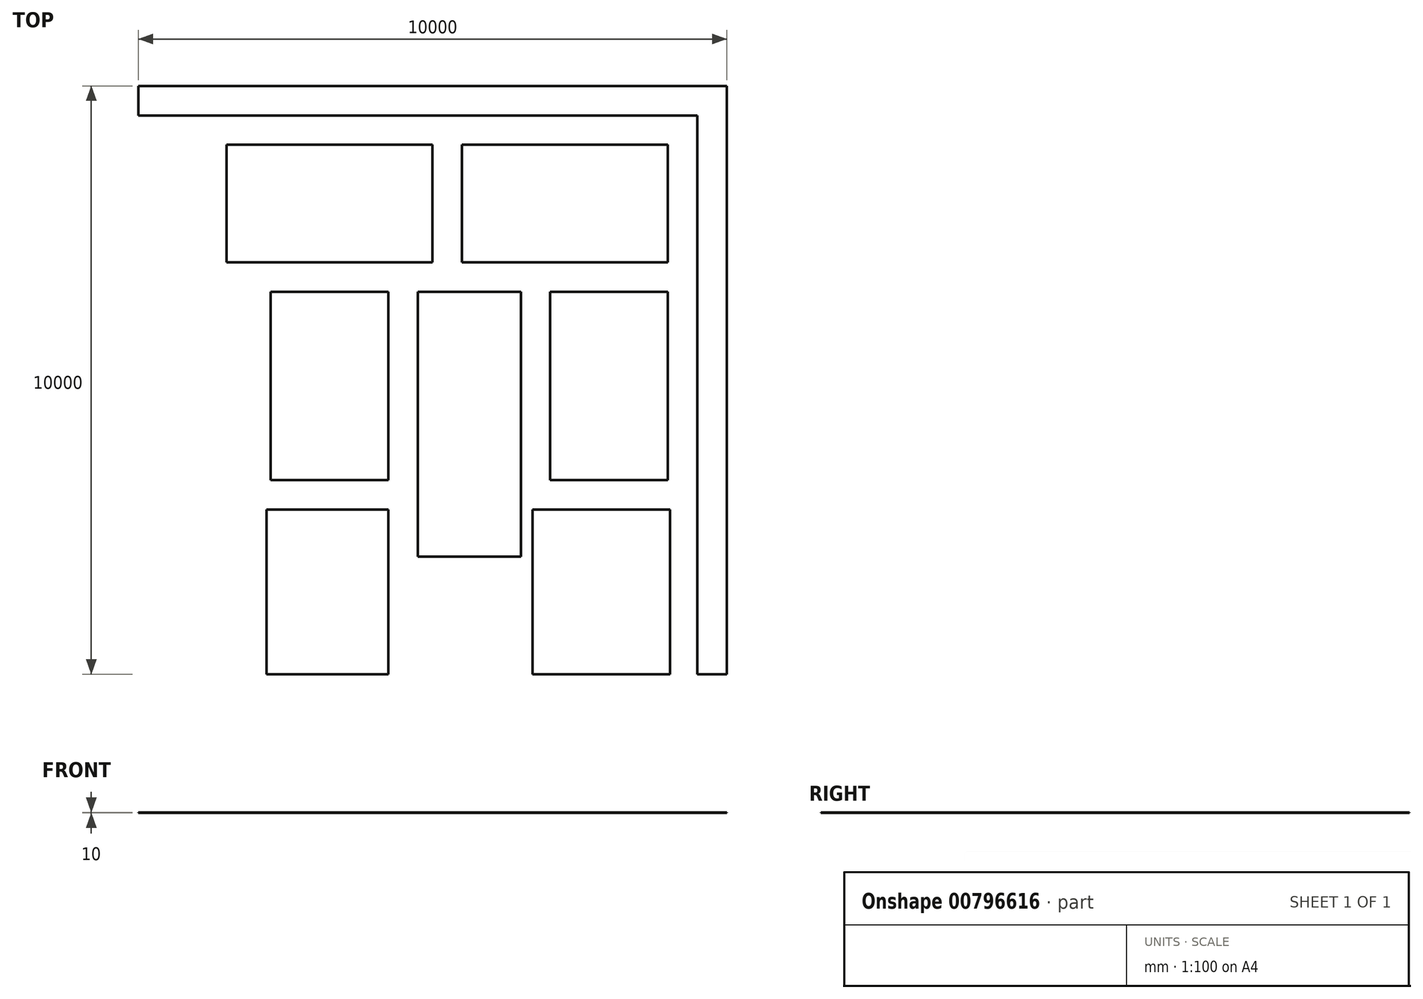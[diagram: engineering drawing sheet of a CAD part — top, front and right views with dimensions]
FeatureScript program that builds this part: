
annotation { "Feature Type Name" : "Feature", "Feature Type Description" : "" }
export const myFeature = defineFeature(function(context is Context, id is Id, definition is map)
    precondition{}
    {
        {
            var Q0;
            Q0=qCreatedBy(makeId("Top.planeOp"),FACE);
            var sketch = newSketch(context, id + "F0", { "sketchPlane" : qUnion([Q0])});
            skLineSegment(sketch, "E0.bottom", {"start": v(5000, -5000) * mm, "end": v(-5000, -5000) * mm});
            skLineSegment(sketch, "E0.top", {"start": v(5000, 5000) * mm, "end": v(-5000, 5000) * mm});
            skLineSegment(sketch, "E0.left", {"start": v(5000, -5000) * mm, "end": v(5000, 5000) * mm});
            skLineSegment(sketch, "E0.right", {"start": v(-5000, -5000) * mm, "end": v(-5000, 5000) * mm});
            skPoint(sketch, "E0.middle", {"position": v(0, 0) * mm});
            skSolve(sketch);
        }
        {
            var Q0;
            Q0=makeQuery(id+"F0.imprint","IMPRINT",FACE,{"disambiguationData":[TD([[makeQuery(id+"F0.imprint","IMPRINT",EDGE,{"derivedFrom":sQuery(id+"F0.wireOp",EDGE,"E0.bottom")}),-1.0]])]});
            var sketch = newSketch(context, id + "F1", { "sketchPlane" : qUnion([Q0])});
            skLineSegment(sketch, "E1", {"start": v(4500, -5000) * mm, "end": v(4500, 4500) * mm});
            skLineSegment(sketch, "E2", {"start": v(4500, 4500) * mm, "end": v(-5000, 4500) * mm});
            skLineSegment(sketch, "E3", {"start": v(4500, -250) * mm, "end": v(5000, -250) * mm, "construction": true});
            skLineSegment(sketch, "E4", {"start": v(-250, 4500) * mm, "end": v(-250, 5000) * mm, "construction": true});
            skSolve(sketch);
        }
        {
            var Q0;
            {var subQ0=sQuery(id+"F1.wireOp",EDGE,"E1");Q0=makeQuery(id+"F1.imprint","IMPRINT",FACE,{"disambiguationData":[TD([[makeQuery(id+"F1.imprint","IMPRINT",EDGE,{"derivedFrom":subQ0}),1.0]])]});}
            var sketch = newSketch(context, id + "F2", { "sketchPlane" : qUnion([Q0])});
            skLineSegment(sketch, "E5.bottom", {"start": v(4000, 4000) * mm, "end": v(500, 4000) * mm});
            skLineSegment(sketch, "E5.top", {"start": v(4000, 2000) * mm, "end": v(500, 2000) * mm});
            skLineSegment(sketch, "E5.left", {"start": v(4000, 4000) * mm, "end": v(4000, 2000) * mm});
            skLineSegment(sketch, "E5.right", {"start": v(500, 4000) * mm, "end": v(500, 2000) * mm});
            skLineSegment(sketch, "E6.bottom", {"start": v(0, 2000) * mm, "end": v(-3500, 2000) * mm});
            skLineSegment(sketch, "E6.top", {"start": v(0, 4000) * mm, "end": v(-3500, 4000) * mm});
            skLineSegment(sketch, "E6.left", {"start": v(0, 2000) * mm, "end": v(0, 4000) * mm});
            skLineSegment(sketch, "E6.right", {"start": v(-3500, 2000) * mm, "end": v(-3500, 4000) * mm});
            skLineSegment(sketch, "E7", {"start": v(0, 3000) * mm, "end": v(500, 3000) * mm, "construction": true});
            skLineSegment(sketch, "E8.0", {"start": v(4500, 4500) * mm, "end": v(-5000, 4500) * mm});
            skLineSegment(sketch, "E9", {"start": v(2250, 4000) * mm, "end": v(2250, 4500) * mm, "construction": true});
            skLineSegment(sketch, "E10.0", {"start": v(4500, -5000) * mm, "end": v(4500, 4500) * mm});
            skLineSegment(sketch, "E11", {"start": v(4000, 3000) * mm, "end": v(4500, 3000) * mm, "construction": true});
            skLineSegment(sketch, "E12.bottom", {"start": v(2000, 1500) * mm, "end": v(4000, 1500) * mm});
            skLineSegment(sketch, "E12.top", {"start": v(2000, -1700) * mm, "end": v(4000, -1700) * mm});
            skLineSegment(sketch, "E12.left", {"start": v(2000, 1500) * mm, "end": v(2000, -1700) * mm});
            skLineSegment(sketch, "E12.right", {"start": v(4000, 1500) * mm, "end": v(4000, -1700) * mm});
            skLineSegment(sketch, "E13", {"start": v(4000, -100) * mm, "end": v(4500, -100) * mm, "construction": true});
            skLineSegment(sketch, "E14", {"start": v(3000, 1500) * mm, "end": v(3000, 2000) * mm, "construction": true});
            skLineSegment(sketch, "E15.bottom", {"start": v(1500, 1500) * mm, "end": v(-250, 1500) * mm});
            skLineSegment(sketch, "E15.top", {"start": v(1500, -3000) * mm, "end": v(-250, -3000) * mm});
            skLineSegment(sketch, "E15.left", {"start": v(1500, 1500) * mm, "end": v(1500, -3000) * mm});
            skLineSegment(sketch, "E15.right", {"start": v(-250, 1500) * mm, "end": v(-250, -3000) * mm});
            skLineSegment(sketch, "E16", {"start": v(1500, 596.76) * mm, "end": v(2000, 596.76) * mm, "construction": true});
            skLineSegment(sketch, "E17.bottom", {"start": v(-750, 1500) * mm, "end": v(-2750, 1500) * mm});
            skLineSegment(sketch, "E17.top", {"start": v(-750, -1700) * mm, "end": v(-2750, -1700) * mm});
            skLineSegment(sketch, "E17.left", {"start": v(-750, 1500) * mm, "end": v(-750, -1700) * mm});
            skLineSegment(sketch, "E17.right", {"start": v(-2750, 1500) * mm, "end": v(-2750, -1700) * mm});
            skLineSegment(sketch, "E18", {"start": v(-750, -920.2) * mm, "end": v(-250, -920.2) * mm, "construction": true});
            skLineSegment(sketch, "E19.bottom", {"start": v(-750, -2200) * mm, "end": v(-2823.75, -2200) * mm});
            skLineSegment(sketch, "E19.top", {"start": v(-750, -5000) * mm, "end": v(-2823.75, -5000) * mm});
            skLineSegment(sketch, "E19.left", {"start": v(-750, -2200) * mm, "end": v(-750, -5000) * mm});
            skLineSegment(sketch, "E19.right", {"start": v(-2823.75, -2200) * mm, "end": v(-2823.75, -5000) * mm});
            skLineSegment(sketch, "E20.0", {"start": v(5000, -5000) * mm, "end": v(-5000, -5000) * mm});
            skLineSegment(sketch, "E21.bottom", {"start": v(1700, -2200) * mm, "end": v(4035.39, -2200) * mm});
            skLineSegment(sketch, "E21.top", {"start": v(1700, -5000) * mm, "end": v(4035.39, -5000) * mm});
            skLineSegment(sketch, "E21.left", {"start": v(1700, -2200) * mm, "end": v(1700, -5000) * mm});
            skLineSegment(sketch, "E21.right", {"start": v(4035.39, -2200) * mm, "end": v(4035.39, -5000) * mm});
            skLineSegment(sketch, "E22", {"start": v(-750, -3600) * mm, "end": v(1700, -3600) * mm, "construction": true});
            skLineSegment(sketch, "E23", {"start": v(2867.7, -2200) * mm, "end": v(2867.7, -1700) * mm, "construction": true});
            skSolve(sketch);
        }
        {
            var Q0;
            Q0=makeQuery(id+"F2.imprint","IMPRINT",FACE,{"disambiguationData":[TD([[makeQuery(id+"F2.imprint","IMPRINT",EDGE,{"derivedFrom":sQuery(id+"F2.wireOp",EDGE,"E19.bottom")}),1.0]])]});
            var Q1;
            Q1=makeQuery(id+"F2.imprint","IMPRINT",FACE,{"disambiguationData":[TD([[makeQuery(id+"F2.imprint","IMPRINT",EDGE,{"derivedFrom":sQuery(id+"F2.wireOp",EDGE,"E21.bottom")}),-1.0]])]});
            var Q2;
            Q2=makeQuery(id+"F2.imprint","IMPRINT",FACE,{"disambiguationData":[TD([[makeQuery(id+"F2.imprint","IMPRINT",EDGE,{"derivedFrom":sQuery(id+"F2.wireOp",EDGE,"E15.bottom")}),1.0]])]});
            var Q3;
            Q3=makeQuery(id+"F2.imprint","IMPRINT",FACE,{"disambiguationData":[TD([[makeQuery(id+"F2.imprint","IMPRINT",EDGE,{"derivedFrom":sQuery(id+"F2.wireOp",EDGE,"E12.bottom")}),-1.0]])]});
            var Q4;
            Q4=makeQuery(id+"F2.imprint","IMPRINT",FACE,{"disambiguationData":[TD([[makeQuery(id+"F2.imprint","IMPRINT",EDGE,{"derivedFrom":sQuery(id+"F2.wireOp",EDGE,"E17.bottom")}),1.0]])]});
            var Q5;
            Q5=makeQuery(id+"F2.imprint","IMPRINT",FACE,{"disambiguationData":[TD([[makeQuery(id+"F2.imprint","IMPRINT",EDGE,{"derivedFrom":sQuery(id+"F2.wireOp",EDGE,"E6.bottom")}),-1.0]])]});
            var Q6;
            Q6=makeQuery(id+"F2.imprint","IMPRINT",FACE,{"disambiguationData":[TD([[makeQuery(id+"F2.imprint","IMPRINT",EDGE,{"derivedFrom":sQuery(id+"F2.wireOp",EDGE,"E5.bottom")}),1.0]])]});
            extrude(context, id + "F3", {"entities" : qUnion([Q0, Q1, Q2, Q3, Q4, Q5, Q6]), "depth" : 10 * mm, "offsetDistance" : 25 * mm});
        }
        {
            var Q0;
            {var subQ3=sQuery(id+"F1.wireOp",EDGE,"E1");Q0=makeQuery(id+"F1.imprint","IMPRINT",FACE,{"disambiguationData":[TD([[makeQuery(id+"F1.imprint","IMPRINT",EDGE,{"derivedFrom":subQ3}),-1.0]])]});}
            extrude(context, id + "F4", {"entities" : qUnion([Q0]), "depth" : 10 * mm, "offsetDistance" : 25 * mm});
        }
        {
            var Q0;
            Q0=sQuery(id+"F0.wireOp",EDGE,"E0.bottom");
            var Q1;
            Q1=sQuery(id+"F0.wireOp",EDGE,"E0.right");
            var Q2;
            Q2=sQuery(id+"F0.wireOp",EDGE,"E0.left");
            var Q3;
            Q3=sQuery(id+"F0.wireOp",EDGE,"E0.top");
            extrude(context, id + "F5", {"bodyType" : ToolBodyType.SURFACE, "surfaceEntities" : qUnion([Q0, Q1, Q2, Q3]), "depth" : 5 * mm, "offsetDistance" : 25 * mm});
        }
    });
